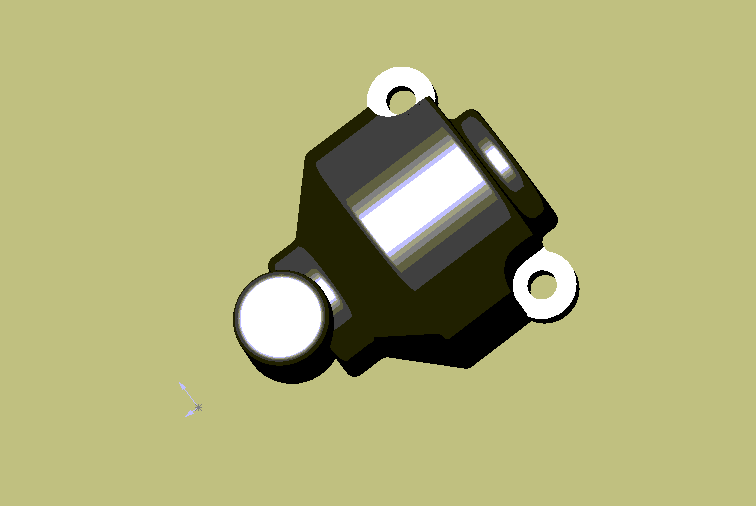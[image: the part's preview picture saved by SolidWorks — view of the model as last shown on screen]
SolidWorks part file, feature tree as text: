
SOLIDWORKS PART (.sldprt)
format: sldprt  version: not decoded by parser v0  size: 359,936 bytes
history: native  units: mm
features: sketch x11, cut_extrude x4, extrude x4, plane x3, cut_revolve x2, material x1, revolve x1, fillet x1 (+8 scaffold rows collapsed)
feature tree (35):
  scaffold x8  (default folders/planes/origin — collapsed)
  material  "Matériau <non spécifié>"
  plane  "Plane1"
  plane  "Plane2"
  plane  "Plane3"
  sketch  "Esquisse1"  dims[c1.D1=7.0mm c1.D6=7.0mm c1.D7=3.5mm c1.D2=~3.437668mm c1.D8=3.5mm c1.D9=3.5mm c1.D10=3.5mm c2.D2=11.0mm c2.D3=15.0mm c2.D4=~7.335312mm c3.D4=45.0deg c3.D5=3.0mm c3.D6=7.5mm c3.D1=8.0mm c4.D6=3.0mm c4.D1=6.0mm c4.D2=8.0mm c4.D4=20.0mm c5.D1=4.0mm c5.D2=6.0mm c5.D3=11.0mm c5.D4=~20.022765mm c5.D5=24.5mm c5.D6=20.0mm c5.D7=39.0mm c6.D2=~17.486229mm c6.D3=11.0mm c6.D5=18.0mm c7.D2=11.0mm c7.D3=6.0mm c7.D4=15.0mm c7.D5=18.0mm c7.D9=2.0mm c7.D1=~7.969447mm c8.D2=6.0mm c8.D3=~3.999991mm c8.D4=~3.999991mm c8.D5=6.0mm c8.D6=~7.969447mm c8.D7=~20.999991mm c8.D8=~20.999991mm c8.D11=24.5mm c8.D12=24.5mm c8.D13=2.0mm c8.D14=~19.77102mm c8.D15=15.0mm c8.D16=~6.283269mm c8.D17=~6.283269mm c8.D18=~4.49712mm c8.D19=~4.49712mm c8.D20=~17.626802mm c8.D21=~3.364452mm c8.D22=~2.991264mm c8.D23=~3.040627mm c8.D24=~3.413825mm c8.D25=7.5mm c8.D26=14.0mm c9.D13=~2.000009mm c9.D14=~14.999995mm c9.D20=15.0mm c10.D13=~2.000006mm c10.D11=7.5mm c10.D12=3.0mm c10.D4=~26.499991mm]
  sketch  "Esquisse2"  dims[c1.D1=4.0mm c1.D2=10.0mm c1.D3=3.0mm c1.D4=2.0mm c1.D5=6.0mm c1.D6=5.5mm c1.D7=11.5mm c1.D8=5.5mm c2.D4=16.0mm]
  revolve  "Base-Révolution"  Angle=180deg
  sketch  "Esquisse3"  dims[D1=6.0mm]
  cut_extrude  "Enlèv. mat.-Extru.1"  [1 undecoded]
  cut_revolve  "Enlèvement de matière-Révolution2"  Angle=360deg
  sketch  "Esquisse11"  dims[D1=10.0mm D2=4.0mm]
  extrude  "Boss.-Extru.5"  Depth=10mm
  sketch  "Esquisse13"  dims[D1=2.0mm]
  sketch  "Esquisse14"  dims[c1.D5=~15.411689mm c1.D2=7.0mm c1.D1=21.0mm c2.D2=21.0mm c2.D3=12.0mm c2.D4=12.0mm]
  extrude  "Boss.-Extru.6"  [1 undecoded]
  sketch  "Esquisse15"
  cut_revolve  "Enlèvement de matière-Révolution3"  Angle=360deg
  sketch  "Esquisse16"
  extrude  "Boss.-Extru.7"  Depth=2.5mm
  sketch  "Esquisse17"  dims[D1=6.0mm D2=6.0mm]
  cut_extrude  "Enlèv. mat.-Extru.8"  Depth=52.5mm
  sketch  "Esquisse18"
  extrude  "Boss.-Extru.8"  Depth=3mm
  cut_extrude  "Enlèv. mat.-Extru.9"  Depth=8mm
  fillet  "Congé7"  Radius=1mm
  sketch  "Esquisse19"  dims[D1=3.0mm D2=3.0mm]
  cut_extrude  "Enlèv. mat.-Extru.10"  [1 undecoded]
decode coverage: 17 of 23 modeling features carry decoded parameters
note: ~ marks probable driven/reference dimensions
note: 3 parameter values undecoded
summary: no parameter record found for 3 features
note: suppression state not decoded; provenance and decode notes live in map.json
